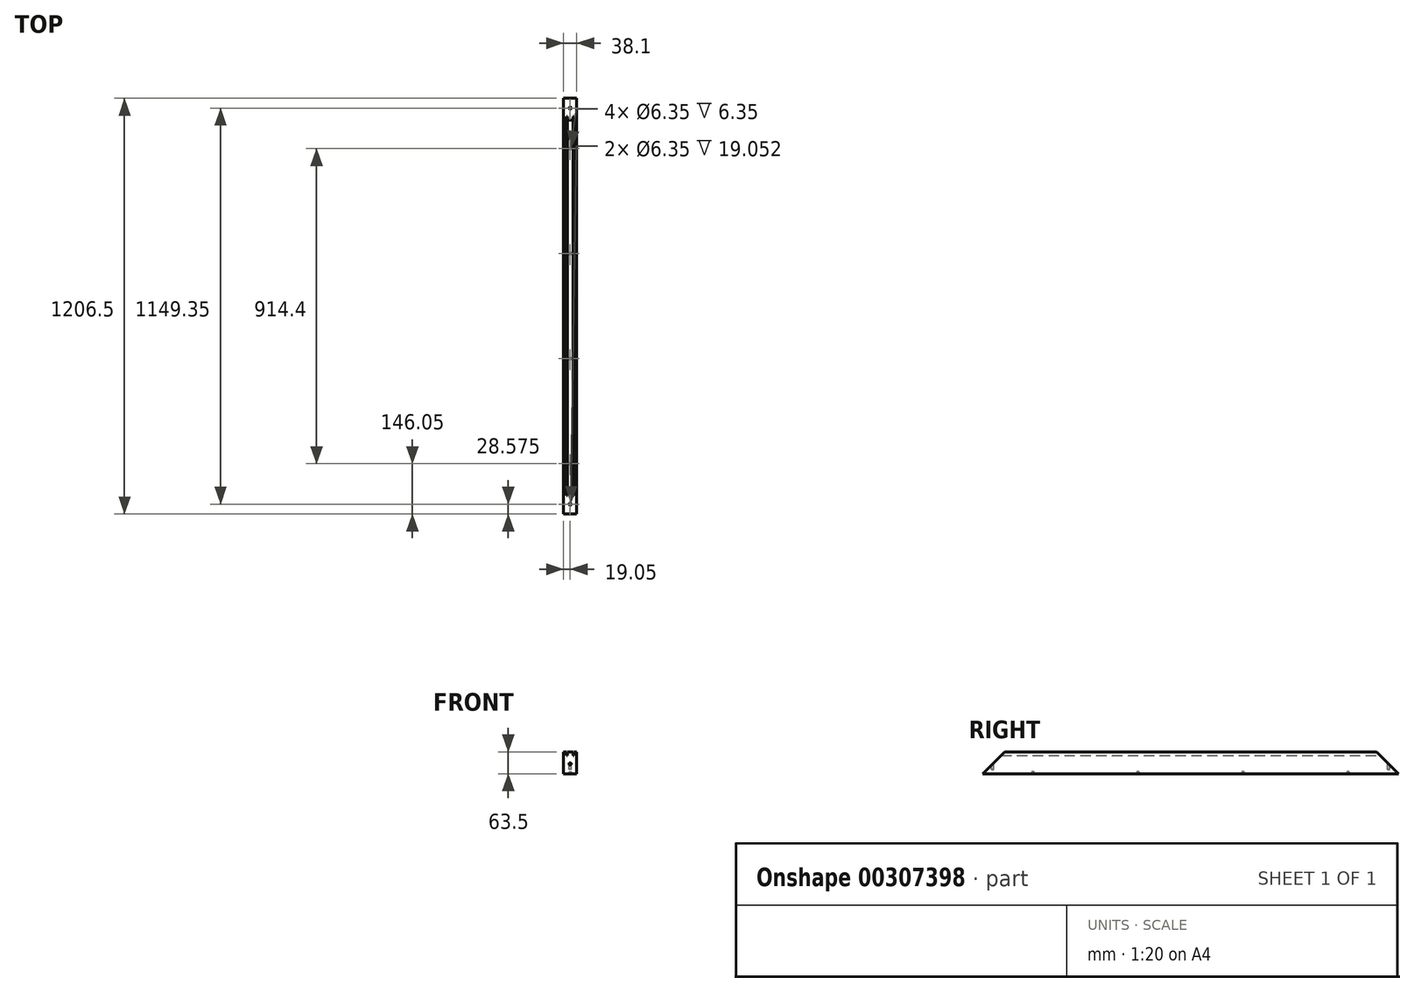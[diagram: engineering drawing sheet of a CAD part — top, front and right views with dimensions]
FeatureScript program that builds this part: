
annotation { "Feature Type Name" : "Feature", "Feature Type Description" : "" }
export const myFeature = defineFeature(function(context is Context, id is Id, definition is map)
    precondition{}
    {
        {
            var Q0;
            Q0=qCreatedBy(makeId("Front.planeOp"),FACE);
            var sketch = newSketch(context, id + "F0", { "sketchPlane" : qUnion([Q0])});
            skLineSegment(sketch, "E0.bottom", {"start": v(19.05, -31.75) * mm, "end": v(-19.05, -31.75) * mm});
            skLineSegment(sketch, "E0.top", {"start": v(19.05, 31.75) * mm, "end": v(-19.05, 31.75) * mm});
            skLineSegment(sketch, "E0.left", {"start": v(19.05, -31.75) * mm, "end": v(19.05, 31.75) * mm});
            skLineSegment(sketch, "E0.right", {"start": v(-19.05, -31.75) * mm, "end": v(-19.05, 31.75) * mm});
            skPoint(sketch, "E0.middle", {"position": v(0, 0) * mm});
            skLineSegment(sketch, "E1.bottom", {"start": v(11.11, 21.59) * mm, "end": v(7.94, 21.59) * mm});
            skLineSegment(sketch, "E1.top", {"start": v(11.11, 31.75) * mm, "end": v(7.94, 31.75) * mm});
            skLineSegment(sketch, "E1.left", {"start": v(11.11, 21.59) * mm, "end": v(11.11, 31.75) * mm});
            skLineSegment(sketch, "E1.right", {"start": v(7.94, 21.59) * mm, "end": v(7.94, 31.75) * mm});
            skPoint(sketch, "E1.middle", {"position": v(9.53, 26.67) * mm});
            skLineSegment(sketch, "E2.bottom", {"start": v(-7.94, 21.59) * mm, "end": v(-11.11, 21.59) * mm});
            skLineSegment(sketch, "E2.top", {"start": v(-7.94, 31.75) * mm, "end": v(-11.11, 31.75) * mm});
            skLineSegment(sketch, "E2.left", {"start": v(-7.94, 21.59) * mm, "end": v(-7.94, 31.75) * mm});
            skLineSegment(sketch, "E2.right", {"start": v(-11.11, 21.59) * mm, "end": v(-11.11, 31.75) * mm});
            skPoint(sketch, "E2.middle", {"position": v(-9.53, 26.67) * mm});
            skSolve(sketch);
        }
        {
            var Q0;
            Q0=makeQuery(id+"F0.imprint","IMPRINT",FACE,{"disambiguationData":[TD([[makeQuery(id+"F0.imprint","IMPRINT",EDGE,{"derivedFrom":sQuery(id+"F0.wireOp",EDGE,"E0.bottom")}),-1.0]])]});
            extrude(context, id + "F1", {"entities" : qUnion([Q0]), "endBound" : BoundingType.SYMMETRIC, "depth" : 1206.5 * mm});
        }
        {
            var Q0;
            Q0=makeQuery(id+"F1.opExtrude","SWEPT_FACE",FACE,{"disambiguationData":[OSD([sQuery(id+"F0.wireOp",EDGE,"E0.left")])]});
            var sketch = newSketch(context, id + "F2", { "sketchPlane" : qUnion([Q0])});
            skLineSegment(sketch, "E3", {"start": v(539.75, 31.75) * mm, "end": v(603.25, -31.75) * mm});
            skLineSegment(sketch, "E4", {"start": v(603.25, -31.75) * mm, "end": v(603.25, 31.75) * mm});
            skLineSegment(sketch, "E5", {"start": v(603.25, 31.75) * mm, "end": v(539.75, 31.75) * mm});
            skLineSegment(sketch, "E6.MirrorCS", {"start": v(-603.25, -31.75) * mm, "end": v(-603.25, 31.75) * mm});
            skLineSegment(sketch, "E7.MirrorCS", {"start": v(-603.25, 31.75) * mm, "end": v(-539.75, 31.75) * mm});
            skLineSegment(sketch, "E8.MirrorCS", {"start": v(-539.75, 31.75) * mm, "end": v(-603.25, -31.75) * mm});
            skSolve(sketch);
        }
        {
            var Q0;
            {var subQ0=sQuery(id+"F0.wireOp",EDGE,"E0.top");Q0=makeQuery(id+"F1.opExtrude","SWEPT_FACE",FACE,{"disambiguationData":[OSD([subQ0]),TDD([makeQuery(id+"F0.imprint","IMPRINT",EDGE,{"disambiguationData":[TD([[makeQuery(id+"F0.imprint","INTERSECT",VERTEX,{"derivedFrom":[subQ0,sQuery(id+"F0.wireOp",EDGE,"E1.top"),sQuery(id+"F0.wireOp",EDGE,"E1.right")]}),-1.0]])],"derivedFrom":subQ0})])]});}
            var sketch = newSketch(context, id + "F3", { "sketchPlane" : qUnion([Q0])});
            skCircle(sketch, "E9", {"center": v(0, 574.68) * mm, "radius": 3.18 * mm});
            skCircle(sketch, "E10.MirrorC", {"center": v(0, -574.68) * mm, "radius": 3.18 * mm});
            skSolve(sketch);
        }
        {
            var Q0;
            Q0 = qSketchRegion(id + "F3", true);
            extrude(context, id + "F4", {"entities" : qUnion([Q0]), "operationType" : NewBodyOperationType.REMOVE, "oppositeDirection" : true, "depth" : 50.8 * mm});
        }
        {
            var Q0;
            Q0 = qSketchRegion(id + "F2", true);
            extrude(context, id + "F5", {"entities" : qUnion([Q0]), "operationType" : NewBodyOperationType.REMOVE, "oppositeDirection" : true, "depth" : 50.8 * mm});
        }
        {
            var Q0;
            Q0=makeQuery(id+"F1.opExtrude","SWEPT_FACE",FACE,{"disambiguationData":[OSD([sQuery(id+"F0.wireOp",EDGE,"E0.bottom")])]});
            var sketch = newSketch(context, id + "F6", { "sketchPlane" : qUnion([Q0])});
            skCircle(sketch, "E11", {"center": v(0, -457.2) * mm, "radius": 3.17 * mm});
            skCircle(sketch, "E12", {"center": v(0, -152.4) * mm, "radius": 3.17 * mm});
            skCircle(sketch, "E13", {"center": v(0, 152.4) * mm, "radius": 3.17 * mm});
            skCircle(sketch, "E14", {"center": v(0, 457.2) * mm, "radius": 3.17 * mm});
            skLineSegment(sketch, "E15", {"start": v(-19.05, 0) * mm, "end": v(19.05, 0) * mm, "construction": true});
            skSolve(sketch);
        }
        {
            var Q0;
            Q0 = qSketchRegion(id + "F6", true);
            extrude(context, id + "F7", {"entities" : qUnion([Q0]), "operationType" : NewBodyOperationType.REMOVE, "oppositeDirection" : true, "depth" : 6.35 * mm});
        }
    });
